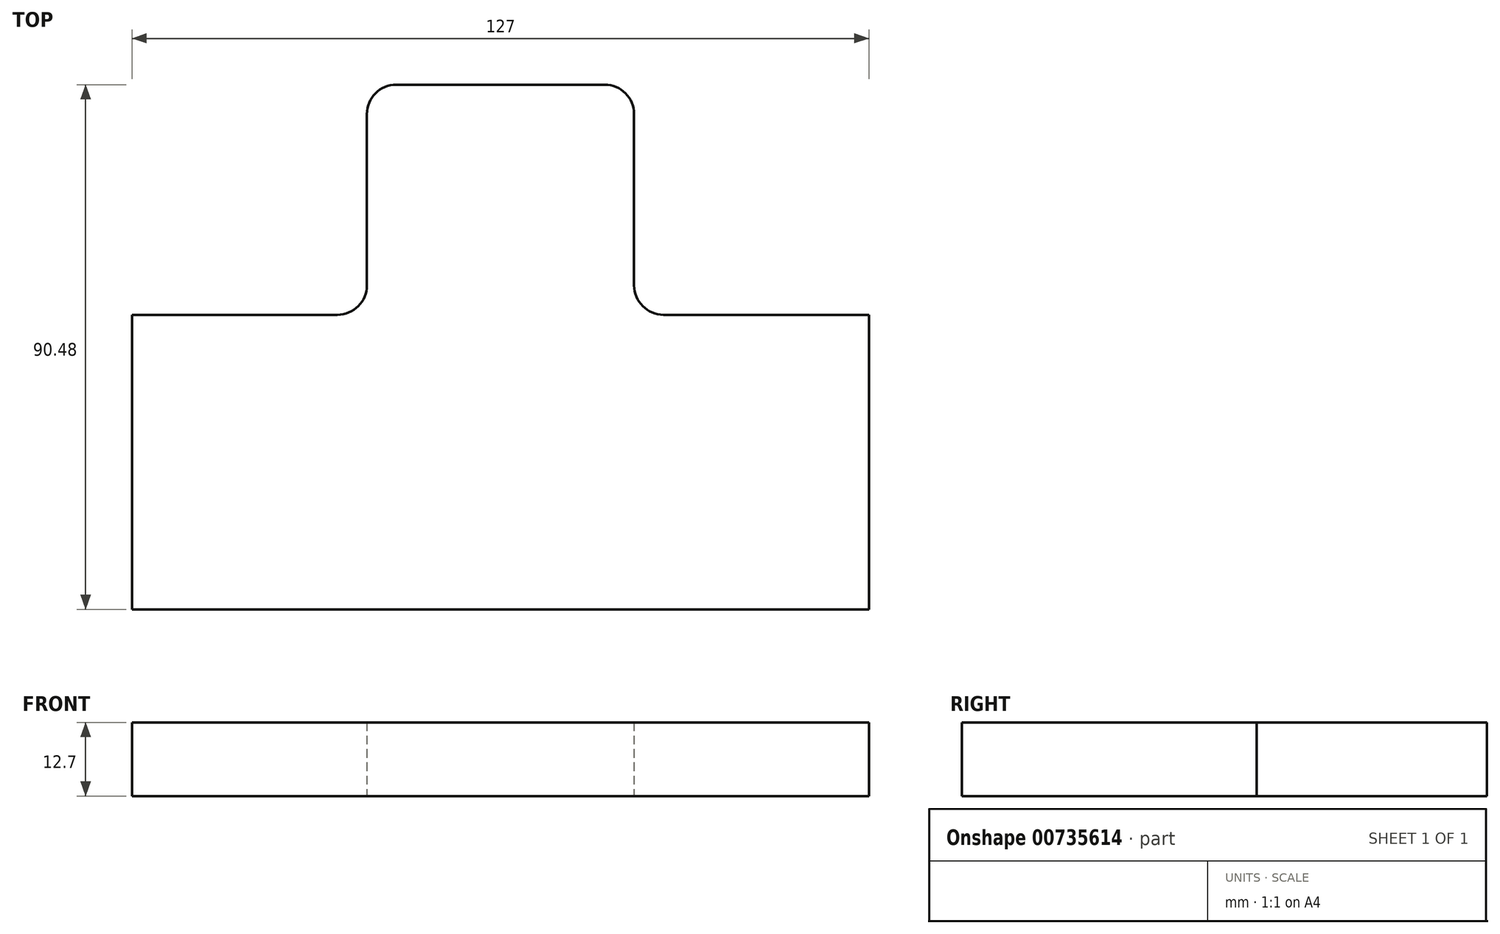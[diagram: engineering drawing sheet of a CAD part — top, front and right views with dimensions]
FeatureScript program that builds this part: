
annotation { "Feature Type Name" : "Feature", "Feature Type Description" : "" }
export const myFeature = defineFeature(function(context is Context, id is Id, definition is map)
    precondition{}
    {
        {
            var Q0;
            Q0=qCreatedBy(makeId("Top.planeOp"),FACE);
            var sketch = newSketch(context, id + "F0", { "sketchPlane" : qUnion([Q0])});
            skLineSegment(sketch, "E0.bottom", {"start": v(23.03, -19.84) * mm, "end": v(-23.03, -19.84) * mm});
            skLineSegment(sketch, "E0.top", {"start": v(23.03, 19.84) * mm, "end": v(-23.03, 19.84) * mm});
            skLineSegment(sketch, "E0.left", {"start": v(23.03, -19.84) * mm, "end": v(23.03, 19.84) * mm});
            skLineSegment(sketch, "E0.right", {"start": v(-23.03, -19.84) * mm, "end": v(-23.03, 19.84) * mm});
            skPoint(sketch, "E0.middle", {"position": v(0, 0) * mm});
            skLineSegment(sketch, "E1.bottom", {"start": v(63.5, -19.84) * mm, "end": v(-63.5, -19.84) * mm});
            skLineSegment(sketch, "E1.top", {"start": v(63.5, -70.64) * mm, "end": v(-63.5, -70.64) * mm});
            skLineSegment(sketch, "E1.left", {"start": v(63.5, -19.84) * mm, "end": v(63.5, -70.64) * mm});
            skLineSegment(sketch, "E1.right", {"start": v(-63.5, -19.84) * mm, "end": v(-63.5, -70.64) * mm});
            skPoint(sketch, "E1.middle", {"position": v(0, -45.24) * mm});
            skSolve(sketch);
        }
        {
            var Q0;
            Q0 = qSketchRegion(id + "F0", true);
            extrude(context, id + "F1", {"entities" : qUnion([Q0]), "depth" : 12.7 * mm, "offsetDistance" : 25.4 * mm});
        }
        {
            var Q0;
            Q0=makeQuery(id+"F1.opExtrude","SWEPT_EDGE",EDGE,{"disambiguationData":[OSD([sQuery(id+"F0.wireOp",EDGE,"E0.top"),sQuery(id+"F0.wireOp",EDGE,"E0.right")])]});
            var Q1;
            Q1=makeQuery(id+"F1.opExtrude","SWEPT_EDGE",EDGE,{"disambiguationData":[OSD([sQuery(id+"F0.wireOp",EDGE,"E0.top"),sQuery(id+"F0.wireOp",EDGE,"E0.left")])]});
            var Q2;
            Q2=makeQuery(id+"F1.opExtrude","SWEPT_EDGE",EDGE,{"disambiguationData":[OSD([sQuery(id+"F0.wireOp",EDGE,"E0.left"),sQuery(id+"F0.wireOp",EDGE,"E1.bottom")])]});
            var Q3;
            Q3=makeQuery(id+"F1.opExtrude","SWEPT_EDGE",EDGE,{"disambiguationData":[OSD([sQuery(id+"F0.wireOp",EDGE,"E0.right"),sQuery(id+"F0.wireOp",EDGE,"E1.bottom")])]});
            fillet(context, id + "F2", {"entities" : qUnion([Q0, Q1, Q2, Q3]), "radius" : 5.08 * mm, "tangentPropagation" : true, "allowEdgeOverflow" : false});
        }
    });
